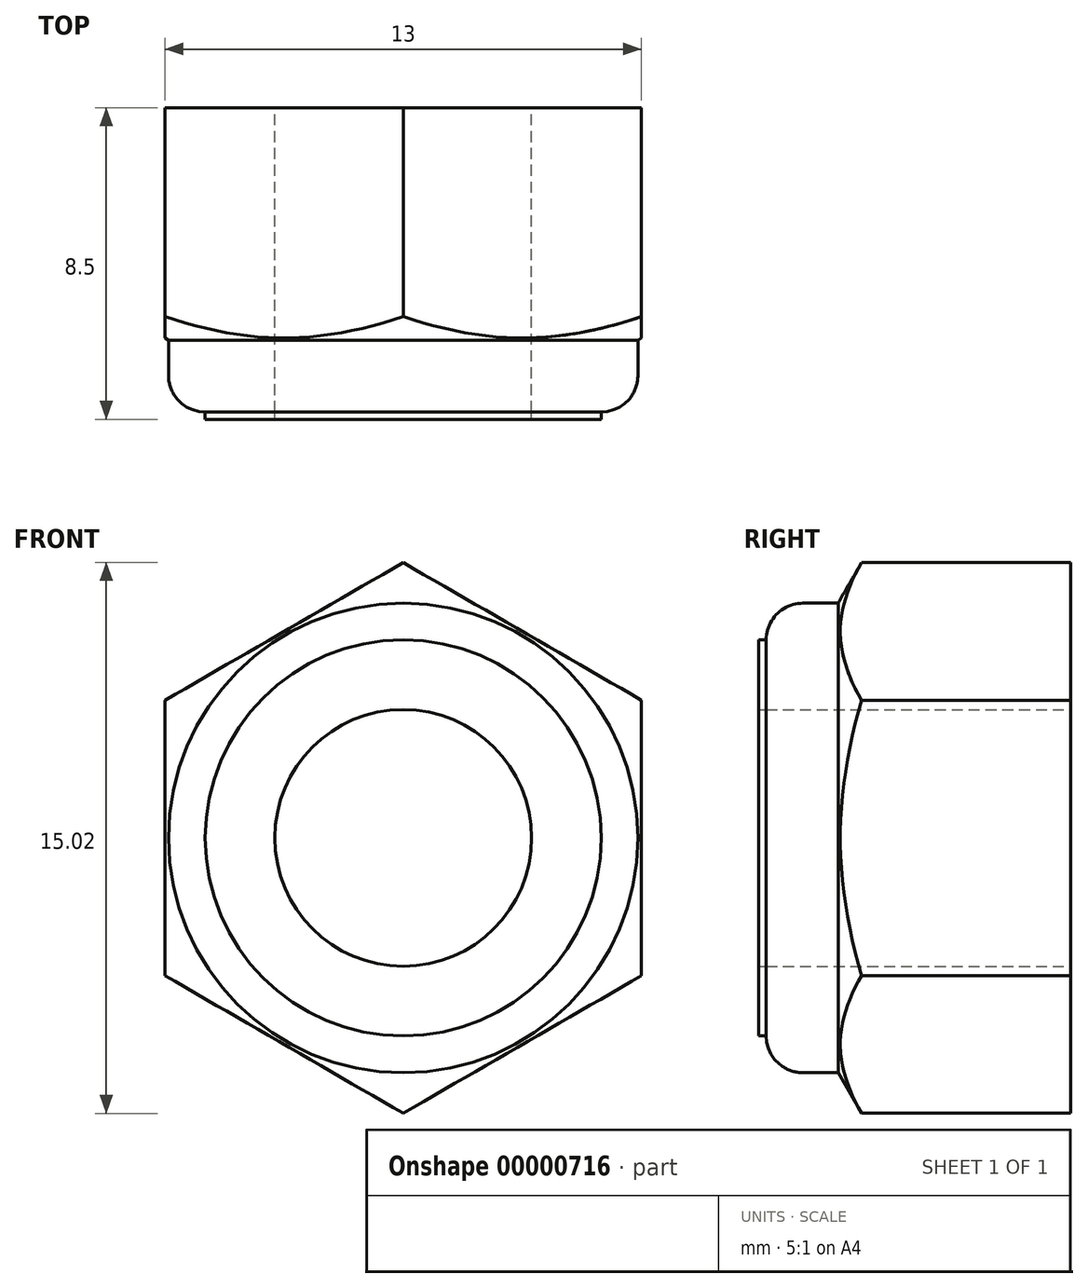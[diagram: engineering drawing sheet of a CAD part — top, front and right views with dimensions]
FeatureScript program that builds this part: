
annotation { "Feature Type Name" : "Feature", "Feature Type Description" : "" }
export const myFeature = defineFeature(function(context is Context, id is Id, definition is map)
    precondition{}
    {
        {
            var Q0;
            Q0=qCreatedBy(makeId("Front.planeOp"),FACE);
            var sketch = newSketch(context, id + "F0", { "sketchPlane" : qUnion([Q0])});
            skCircle(sketch, "E0.cCircle", {"center": v(0, 0) * mm, "radius": 6.5 * mm, "construction": true});
            skLineSegment(sketch, "E0.0", {"start": v(6.5, 3.75) * mm, "end": v(6.5, -3.75) * mm});
            skLineSegment(sketch, "E0.1", {"start": v(6.5, -3.75) * mm, "end": v(0, -7.5) * mm});
            skLineSegment(sketch, "E0.2", {"start": v(0, -7.5) * mm, "end": v(-6.5, -3.75) * mm});
            skLineSegment(sketch, "E0.3", {"start": v(-6.5, -3.75) * mm, "end": v(-6.5, 3.75) * mm});
            skLineSegment(sketch, "E0.4", {"start": v(-6.5, 3.75) * mm, "end": v(0, 7.5) * mm});
            skLineSegment(sketch, "E0.5", {"start": v(0, 7.5) * mm, "end": v(6.5, 3.75) * mm});
            skPoint(sketch, "E0.0.midPoint", {"position": v(6.5, 0) * mm});
            skSolve(sketch);
        }
        {
            var Q0;
            Q0=makeQuery(id+"F0.imprint","IMPRINT",FACE,{"disambiguationData":[TD([[makeQuery(id+"F0.imprint","IMPRINT",EDGE,{"derivedFrom":sQuery(id+"F0.wireOp",EDGE,"E0.0")}),-1.0]])]});
            extrude(context, id + "F1", {"entities" : qUnion([Q0]), "depth" : 7 * mm});
        }
        {
            var Q0;
            Q0=qCreatedBy(makeId("Right.planeOp"),FACE);
            var sketch = newSketch(context, id + "F2", { "sketchPlane" : qUnion([Q0])});
            skLineSegment(sketch, "E1", {"start": v(-5.7, 7.5) * mm, "end": v(-10.03, 0) * mm});
            skLineSegment(sketch, "E2", {"start": v(-10.03, 0) * mm, "end": v(-12.28, 0) * mm});
            skLineSegment(sketch, "E3", {"start": v(-12.28, 0) * mm, "end": v(-12.28, 7.5) * mm});
            skLineSegment(sketch, "E4", {"start": v(-5.7, 7.5) * mm, "end": v(-12.28, 7.5) * mm});
            skLineSegment(sketch, "E5", {"start": v(-10.03, 0) * mm, "end": v(3.9, 0) * mm, "construction": true});
            skSolve(sketch);
        }
        {
            var Q0;
            Q0=makeQuery(id+"F2.imprint","IMPRINT",FACE,{"disambiguationData":[TD([[makeQuery(id+"F2.imprint","IMPRINT",EDGE,{"derivedFrom":sQuery(id+"F2.wireOp",EDGE,"E1")}),-1.0]])]});
            var Q1;
            Q1=sQuery(id+"F2.wireOp",EDGE,"E5");
            revolve(context, id + "F3", {"operationType" : NewBodyOperationType.REMOVE, "entities" : qUnion([Q0]), "axis" : qUnion([Q1]), "revolveType" : RevolveType.FULL, "oppositeDirection" : true});
        }
        {
            var Q0;
            Q0=makeQuery(id+"F1.opExtrude","CAP_FACE",FACE,{"disambiguationData":[OSD([sQuery(id+"F0.wireOp",EDGE,"E0.0"),sQuery(id+"F0.wireOp",EDGE,"E0.1"),sQuery(id+"F0.wireOp",EDGE,"E0.2"),sQuery(id+"F0.wireOp",EDGE,"E0.3"),sQuery(id+"F0.wireOp",EDGE,"E0.4"),sQuery(id+"F0.wireOp",EDGE,"E0.5")])],"isStart":true});
            var sketch = newSketch(context, id + "F4", { "sketchPlane" : qUnion([Q0])});
            skCircle(sketch, "E6", {"center": v(0, 0) * mm, "radius": 6.4 * mm});
            skSolve(sketch);
        }
        {
            var Q0;
            Q0=makeQuery(id+"F4.imprint","IMPRINT",FACE,{"disambiguationData":[TD([[makeQuery(id+"F4.imprint","IMPRINT",EDGE,{"derivedFrom":sQuery(id+"F4.wireOp",EDGE,"E6")}),1.0]])]});
            extrude(context, id + "F5", {"entities" : qUnion([Q0]), "operationType" : NewBodyOperationType.ADD, "oppositeDirection" : true, "depth" : 8.3 * mm});
        }
        {
            var Q0;
            Q0=makeQuery(id+"F5.opExtrude","CAP_EDGE",EDGE,{"disambiguationData":[OSD([sQuery(id+"F4.wireOp",EDGE,"E6")])],"isStart":false});
            fillet(context, id + "F6", {"entities" : qUnion([Q0]), "radius" : 1 * mm, "tangentPropagation" : true, "allowEdgeOverflow" : false});
        }
        {
            var Q0;
            Q0=makeQuery(id+"F5.opExtrude","CAP_FACE",FACE,{"disambiguationData":[OSD([sQuery(id+"F4.wireOp",EDGE,"E6")])],"isStart":false});
            var sketch = newSketch(context, id + "F7", { "sketchPlane" : qUnion([Q0])});
            skCircle(sketch, "E7.0", {"center": v(0, 0) * mm, "radius": 5.4 * mm});
            skSolve(sketch);
        }
        {
            var Q0;
            Q0=makeQuery(id+"F7.imprint","IMPRINT",FACE,{"disambiguationData":[TD([[makeQuery(id+"F7.imprint","IMPRINT",EDGE,{"derivedFrom":sQuery(id+"F7.wireOp",EDGE,"E7.0")}),1.0]])]});
            extrude(context, id + "F8", {"entities" : qUnion([Q0]), "depth" : .2 * mm});
        }
        {
            var Q0;
            Q0=makeQuery(id+"F1.opExtrude","CAP_FACE",FACE,{"disambiguationData":[OSD([sQuery(id+"F0.wireOp",EDGE,"E0.0"),sQuery(id+"F0.wireOp",EDGE,"E0.1"),sQuery(id+"F0.wireOp",EDGE,"E0.2"),sQuery(id+"F0.wireOp",EDGE,"E0.3"),sQuery(id+"F0.wireOp",EDGE,"E0.4"),sQuery(id+"F0.wireOp",EDGE,"E0.5")])],"isStart":true});
            var sketch = newSketch(context, id + "F9", { "sketchPlane" : qUnion([Q0])});
            skCircle(sketch, "E8", {"center": v(0, 0) * mm, "radius": 3.5 * mm});
            skSolve(sketch);
        }
        {
            var Q0;
            Q0=makeQuery(id+"F9.imprint","IMPRINT",FACE,{"disambiguationData":[TD([[makeQuery(id+"F9.imprint","IMPRINT",EDGE,{"derivedFrom":sQuery(id+"F9.wireOp",EDGE,"E8")}),1.0]])]});
            extrude(context, id + "F10", {"entities" : qUnion([Q0]), "operationType" : NewBodyOperationType.REMOVE, "oppositeDirection" : true, "depth" : 25 * mm});
        }
    });
